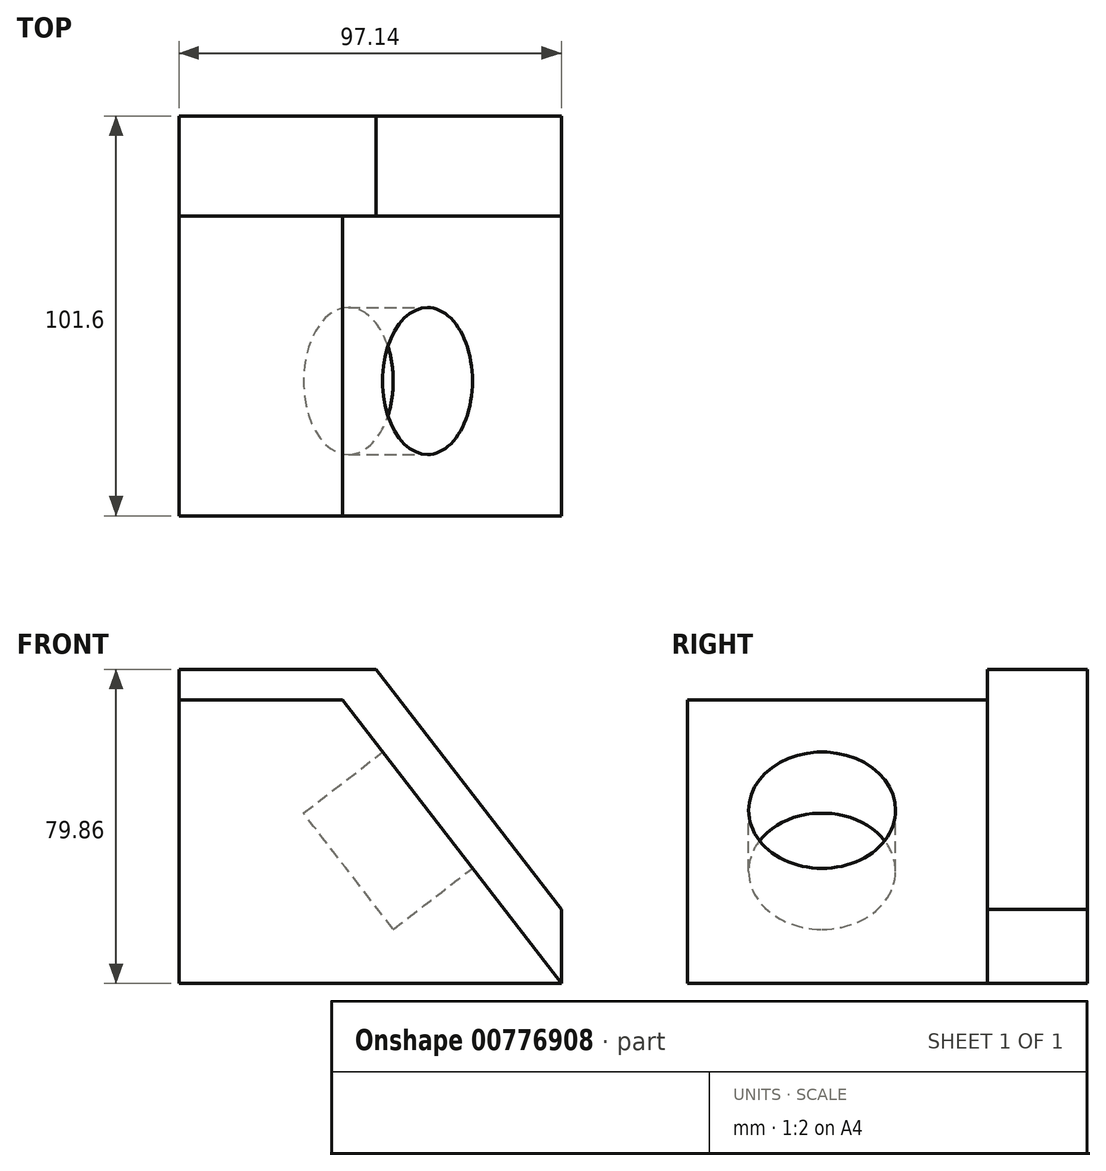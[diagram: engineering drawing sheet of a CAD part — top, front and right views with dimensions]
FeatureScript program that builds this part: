
annotation { "Feature Type Name" : "Feature", "Feature Type Description" : "" }
export const myFeature = defineFeature(function(context is Context, id is Id, definition is map)
    precondition{}
    {
        {
            var Q0;
            Q0=qCreatedBy(makeId("Front.planeOp"),FACE);
            var sketch = newSketch(context, id + "F0", { "sketchPlane" : qUnion([Q0])});
            skLineSegment(sketch, "E0.bottom", {"start": v(1.5, 39.93) * mm, "end": v(-48.57, 39.93) * mm});
            skLineSegment(sketch, "E0.top", {"start": v(48.57, -39.93) * mm, "end": v(-48.57, -39.93) * mm});
            skLineSegment(sketch, "E0.left", {"start": v(48.57, -21.06) * mm, "end": v(48.57, -39.93) * mm});
            skLineSegment(sketch, "E0.right", {"start": v(-48.57, 39.93) * mm, "end": v(-48.57, -39.93) * mm});
            skPoint(sketch, "E0.middle", {"position": v(0, 0) * mm});
            skLineSegment(sketch, "E1", {"start": v(-7.04, 32.14) * mm, "end": v(48.57, -39.93) * mm});
            skLineSegment(sketch, "E2", {"start": v(1.5, 39.93) * mm, "end": v(48.57, -21.06) * mm});
            skPoint(sketch, "E3.orphan", {"position": v(48.57, 39.93) * mm});
            skLineSegment(sketch, "E4", {"start": v(-7.04, 32.14) * mm, "end": v(-48.57, 32.14) * mm});
            skSolve(sketch);
        }
        {
            var Q0;
            Q0=makeQuery(id+"F0.imprint","IMPRINT",FACE,{"disambiguationData":[TD([[makeQuery(id+"F0.imprint","IMPRINT",EDGE,{"derivedFrom":sQuery(id+"F0.wireOp",EDGE,"E0.top")}),-1.0]])]});
            extrude(context, id + "F1", {"entities" : qUnion([Q0]), "depth" : 76.2 * mm, "offsetDistance" : 25.4 * mm});
        }
        {
            var Q0;
            Q0 = qSketchRegion(id + "F0", true);
            extrude(context, id + "F2", {"entities" : qUnion([Q0]), "operationType" : NewBodyOperationType.ADD, "oppositeDirection" : true, "depth" : 25.4 * mm, "offsetDistance" : 25.4 * mm});
        }
        {
            var Q0;
            Q0=makeQuery(id+"F1.opExtrude","SWEPT_FACE",FACE,{"disambiguationData":[OSD([sQuery(id+"F0.wireOp",EDGE,"E1")])]});
            var sketch = newSketch(context, id + "F3", { "sketchPlane" : qUnion([Q0])});
            skCircle(sketch, "E5", {"center": v(-41.96, -5.63) * mm, "radius": 18.66 * mm});
            skSolve(sketch);
        }
        {
            var Q0;
            Q0=makeQuery(id+"F3.imprint","IMPRINT",FACE,{"disambiguationData":[TD([[makeQuery(id+"F3.imprint","IMPRINT",EDGE,{"derivedFrom":sQuery(id+"F3.wireOp",EDGE,"E5")}),1.0]])]});
            extrude(context, id + "F4", {"entities" : qUnion([Q0]), "operationType" : NewBodyOperationType.REMOVE, "oppositeDirection" : true, "depth" : 25.4 * mm, "offsetDistance" : 25.4 * mm});
        }
    });
